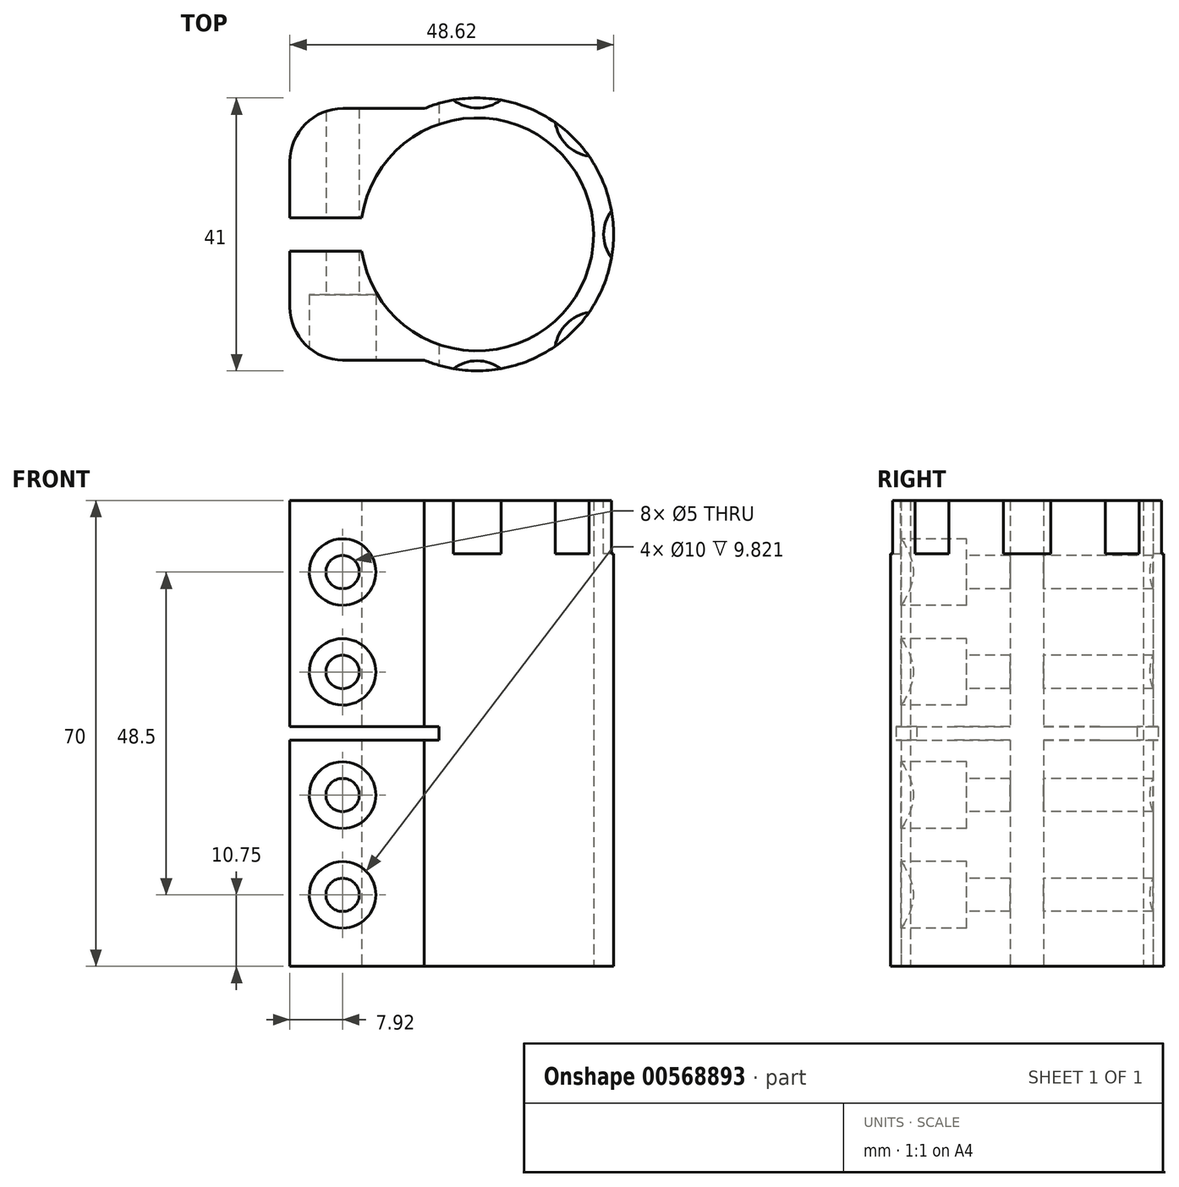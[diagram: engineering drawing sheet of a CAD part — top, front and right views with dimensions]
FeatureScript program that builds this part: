
annotation { "Feature Type Name" : "Feature", "Feature Type Description" : "" }
export const myFeature = defineFeature(function(context is Context, id is Id, definition is map)
    precondition{}
    {
        {
            var Q0;
            Q0=qCreatedBy(makeId("Top.planeOp"),FACE);
            var sketch = newSketch(context, id + "F0", { "sketchPlane" : qUnion([Q0])});
            skArc(sketch, "E0", {"start": v(-7.92, -18.9) * mm, "mid": v(20.5, 0) * mm, "end": v(-7.92, 18.9) * mm});
            skArc(sketch, "E1", {"start": v(-17.32, -2.5) * mm, "mid": v(17.5, 0) * mm, "end": v(-17.32, 2.5) * mm});
            skLineSegment(sketch, "E2", {"start": v(-7.92, 18.9) * mm, "end": v(-20.12, 18.9) * mm});
            skLineSegment(sketch, "E3", {"start": v(-28.12, 10.9) * mm, "end": v(-28.12, 2.5) * mm});
            skLineSegment(sketch, "E4", {"start": v(-28.12, 2.5) * mm, "end": v(-17.32, 2.5) * mm});
            skPoint(sketch, "E5.visualSharp", {"position": v(-28.12, 18.9) * mm});
            skArc(sketch, "E5.filletArc", {"start": v(-20.12, 18.9) * mm, "mid": v(-25.78, 16.57) * mm, "end": v(-28.12, 10.9) * mm});
            skLineSegment(sketch, "E6", {"start": v(0, 0) * mm, "end": v(59.46, 0) * mm, "construction": true});
            skLineSegment(sketch, "E7.MirrorCS", {"start": v(-28.12, -10.9) * mm, "end": v(-28.12, -2.5) * mm});
            skLineSegment(sketch, "E8.MirrorCS", {"start": v(-28.12, -2.5) * mm, "end": v(-17.32, -2.5) * mm});
            skLineSegment(sketch, "E9.MirrorCS", {"start": v(-7.92, -18.9) * mm, "end": v(-20.12, -18.9) * mm});
            skArc(sketch, "E10.MirrorCS", {"start": v(-20.12, -18.9) * mm, "mid": v(-25.78, -16.57) * mm, "end": v(-28.12, -10.9) * mm});
            skSolve(sketch);
        }
        {
            var Q0;
            Q0 = qSketchRegion(id + "F0", true);
            extrude(context, id + "F1", {"entities" : qUnion([Q0]), "endBound" : BoundingType.SYMMETRIC, "depth" : 70 * mm, "offsetDistance" : 25 * mm});
        }
        {
            var Q0;
            Q0=makeQuery(id+"F1.opExtrude","SWEPT_FACE",FACE,{"disambiguationData":[OSD([sQuery(id+"F0.wireOp",EDGE,"E9.MirrorCS")])]});
            var sketch = newSketch(context, id + "F2", { "sketchPlane" : qUnion([Q0])});
            skPoint(sketch, "E11", {"position": v(-20.2, -24.25) * mm});
            skPoint(sketch, "E12", {"position": v(-20.2, -9.25) * mm});
            skPoint(sketch, "E13", {"position": v(-20.2, 9.25) * mm});
            skPoint(sketch, "E14", {"position": v(-20.2, 24.25) * mm});
            skSolve(sketch);
        }
        {
            var Q0;
            Q0=sQuery(id+"F2.wireOp",VERTEX,"E11");
            var Q1;
            Q1=sQuery(id+"F2.wireOp",VERTEX,"E12");
            var Q2;
            Q2=sQuery(id+"F2.wireOp",VERTEX,"E13");
            var Q3;
            Q3=sQuery(id+"F2.wireOp",VERTEX,"E14");
            var Q4;
            Q4=makeQuery(id+"F1.opExtrude","SWEPT_BODY",BODY,{"disambiguationData":[OSD([sQuery(id+"F0.wireOp",EDGE,"E0"),sQuery(id+"F0.wireOp",EDGE,"E1"),sQuery(id+"F0.wireOp",EDGE,"E2"),sQuery(id+"F0.wireOp",EDGE,"E3"),sQuery(id+"F0.wireOp",EDGE,"E4"),sQuery(id+"F0.wireOp",EDGE,"E5.filletArc"),sQuery(id+"F0.wireOp",EDGE,"E7.MirrorCS"),sQuery(id+"F0.wireOp",EDGE,"E8.MirrorCS"),sQuery(id+"F0.wireOp",EDGE,"E9.MirrorCS"),sQuery(id+"F0.wireOp",EDGE,"E10.MirrorCS")])]});
            hole(context, id + "F3", {"style" : HoleStyle.C_BORE, "endStyle" : HoleEndStyle.THROUGH, "holeDiameter" : 5 * mm, "cBoreDiameter" : 10 * mm, "cBoreDepth" : 8 * mm, "majorDiameter" : 5 * mm, "isTappedThrough" : true, "tappedDepth" : 12 * mm, "tapClearance" : 3, "locations" : qUnion([Q0, Q1, Q2, Q3]), "scope" : qUnion([Q4])});
        }
        {
            var Q0;
            Q0=qCreatedBy(makeId("Front.planeOp"),FACE);
            var sketch = newSketch(context, id + "F4", { "sketchPlane" : qUnion([Q0])});
            skLineSegment(sketch, "E15.bottom", {"start": v(-28.12, 1) * mm, "end": v(-5.72, 1) * mm});
            skLineSegment(sketch, "E15.top", {"start": v(-28.12, -1) * mm, "end": v(-5.72, -1) * mm});
            skLineSegment(sketch, "E15.left", {"start": v(-28.12, 1) * mm, "end": v(-28.12, -1) * mm});
            skLineSegment(sketch, "E15.right", {"start": v(-5.72, 1) * mm, "end": v(-5.72, -1) * mm});
            skSolve(sketch);
        }
        {
            var Q0;
            Q0 = qSketchRegion(id + "F4", true);
            extrude(context, id + "F5", {"entities" : qUnion([Q0]), "operationType" : NewBodyOperationType.REMOVE, "endBound" : BoundingType.SYMMETRIC, "oppositeDirection" : true, "depth" : 50 * mm, "offsetDistance" : 25 * mm});
        }
        {
            var Q0;
            Q0=makeQuery(id+"F1.opExtrude","CAP_FACE",FACE,{"disambiguationData":[OSD([sQuery(id+"F0.wireOp",EDGE,"E0"),sQuery(id+"F0.wireOp",EDGE,"E1"),sQuery(id+"F0.wireOp",EDGE,"E2"),sQuery(id+"F0.wireOp",EDGE,"E3"),sQuery(id+"F0.wireOp",EDGE,"E4"),sQuery(id+"F0.wireOp",EDGE,"E5.filletArc"),sQuery(id+"F0.wireOp",EDGE,"E7.MirrorCS"),sQuery(id+"F0.wireOp",EDGE,"E8.MirrorCS"),sQuery(id+"F0.wireOp",EDGE,"E9.MirrorCS"),sQuery(id+"F0.wireOp",EDGE,"E10.MirrorCS")])],"isStart":false});
            var sketch = newSketch(context, id + "F6", { "sketchPlane" : qUnion([Q0])});
            skCircle(sketch, "E16", {"center": v(0, -25) * mm, "radius": 6 * mm});
            skCircle(sketch, "E17.1.0", {"center": v(17.68, -17.68) * mm, "radius": 6 * mm});
            skCircle(sketch, "E17.2.0", {"center": v(25, 0) * mm, "radius": 6 * mm});
            skCircle(sketch, "E17.3.0", {"center": v(17.68, 17.68) * mm, "radius": 6 * mm});
            skCircle(sketch, "E17.4.0", {"center": v(0, 25) * mm, "radius": 6 * mm});
            skPoint(sketch, "E17.center", {"position": v(0, 0) * mm});
            skLineSegment(sketch, "E17.anchor1", {"start": v(0, 0) * mm, "end": v(0, -25) * mm, "construction": true});
            skLineSegment(sketch, "E17.anchor2", {"start": v(0, 0) * mm, "end": v(0, 25) * mm, "construction": true});
            skSolve(sketch);
        }
        {
            var Q0;
            Q0 = qSketchRegion(id + "F6", true);
            extrude(context, id + "F7", {"entities" : qUnion([Q0]), "operationType" : NewBodyOperationType.REMOVE, "oppositeDirection" : true, "depth" : 8 * mm, "offsetDistance" : 25 * mm});
        }
    });
